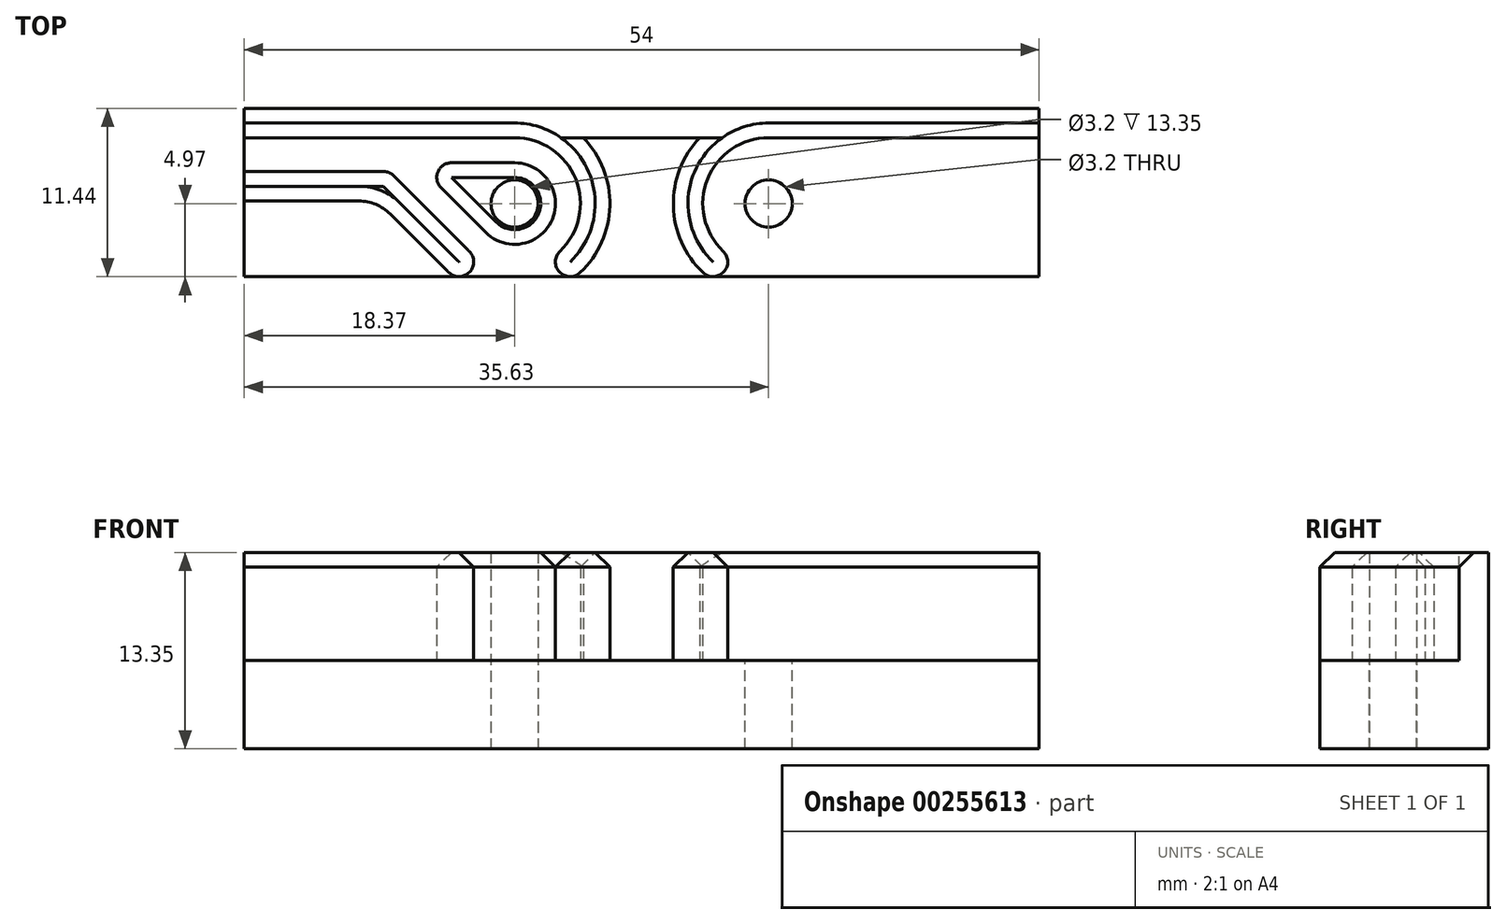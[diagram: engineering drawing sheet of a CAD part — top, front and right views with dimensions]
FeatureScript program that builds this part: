
annotation { "Feature Type Name" : "Feature", "Feature Type Description" : "" }
export const myFeature = defineFeature(function(context is Context, id is Id, definition is map)
    precondition{}
    {
        {
            var Q0;
            Q0=qCreatedBy(makeId("Top.planeOp"),FACE);
            cPlane(context, id + "F0", {"entities" : qUnion([Q0]), "cplaneType" : CPlaneType.OFFSET, "offset" : 6 * mm, "width" : 150 * mm, "height" : 150 * mm});
        }
        {
            var Q0;
            Q0=qCreatedBy(id+"F0.planeOp",FACE);
            var sketch = newSketch(context, id + "F1", { "sketchPlane" : qUnion([Q0])});
            skLineSegment(sketch, "E0.bottom", {"start": v(-27, 6.48) * mm, "end": v(27, 6.48) * mm});
            skLineSegment(sketch, "E0.top", {"start": v(-27, 4.48) * mm, "end": v(-8.63, 4.48) * mm});
            skLineSegment(sketch, "E0.left", {"start": v(-27, 6.48) * mm, "end": v(-27, 4.48) * mm});
            skLineSegment(sketch, "E0.right", {"start": v(27, 6.48) * mm, "end": v(27, 4.48) * mm});
            skArc(sketch, "E1", {"start": v(-10.6, -1.96) * mm, "mid": v(-6.07, -1.06) * mm, "end": v(-8.63, 2.77) * mm});
            skArc(sketch, "E2.MirrorC", {"start": v(10.6, -1.96) * mm, "mid": v(6.07, -1.06) * mm, "end": v(8.63, 2.77) * mm});
            skLineSegment(sketch, "E3", {"start": v(-8.63, 2.77) * mm, "end": v(-12.92, 2.77) * mm});
            skLineSegment(sketch, "E4", {"start": v(-13.62, 1.07) * mm, "end": v(-10.6, -1.96) * mm});
            skArc(sketch, "E5", {"start": v(-12.92, 2.77) * mm, "mid": v(-13.84, 2.16) * mm, "end": v(-13.62, 1.07) * mm});
            skLineSegment(sketch, "E6.MirrorCS", {"start": v(8.63, 2.77) * mm, "end": v(12.92, 2.77) * mm});
            skArc(sketch, "E7.MirrorCS", {"start": v(12.92, 2.77) * mm, "mid": v(13.84, 2.16) * mm, "end": v(13.62, 1.07) * mm});
            skLineSegment(sketch, "E8.MirrorCS", {"start": v(13.62, 1.07) * mm, "end": v(10.6, -1.96) * mm});
            skCircle(sketch, "E9", {"center": v(-8.63, 0) * mm, "radius": 1.6 * mm});
            skCircle(sketch, "E10", {"center": v(8.63, 0) * mm, "radius": 1.6 * mm});
            skLineSegment(sketch, "E11", {"start": v(-27, 2.18) * mm, "end": v(-17.55, 2.18) * mm});
            skLineSegment(sketch, "E12", {"start": v(-16.84, 1.88) * mm, "end": v(-11.8, -3.16) * mm});
            skLineSegment(sketch, "E13", {"start": v(-13.2, -4.58) * mm, "end": v(-17.08, -0.7) * mm});
            skLineSegment(sketch, "E14", {"start": v(-19.2, 0.17) * mm, "end": v(-27, 0.17) * mm});
            skLineSegment(sketch, "E15", {"start": v(-27, 0.17) * mm, "end": v(-27, 2.18) * mm});
            skArc(sketch, "E16", {"start": v(-11.8, -3.16) * mm, "mid": v(-11.76, -3.2) * mm, "end": v(-11.72, -3.24) * mm});
            skArc(sketch, "E17", {"start": v(-13.2, -4.58) * mm, "mid": v(-13.15, -4.63) * mm, "end": v(-13.1, -4.69) * mm});
            skLineSegment(sketch, "E18.trimOffspring", {"start": v(-3.95, 4.48) * mm, "end": v(3.95, 4.48) * mm});
            skPoint(sketch, "E19.visualSharp", {"position": v(-17.13, 2.18) * mm});
            skArc(sketch, "E19.filletArc", {"start": v(-16.84, 1.88) * mm, "mid": v(-17.17, 2.1) * mm, "end": v(-17.55, 2.18) * mm});
            skPoint(sketch, "E20.visualSharp", {"position": v(-17.96, 0.17) * mm});
            skArc(sketch, "E20.filletArc", {"start": v(-17.08, -0.7) * mm, "mid": v(-18.06, -0.05) * mm, "end": v(-19.2, 0.17) * mm});
            skArc(sketch, "E21.MirrorCS", {"start": v(13.2, -4.58) * mm, "mid": v(13.15, -4.63) * mm, "end": v(13.1, -4.69) * mm});
            skArc(sketch, "E22.MirrorCS", {"start": v(11.8, -3.16) * mm, "mid": v(11.76, -3.2) * mm, "end": v(11.72, -3.24) * mm});
            skLineSegment(sketch, "E23.MirrorCS", {"start": v(16.84, 1.88) * mm, "end": v(11.8, -3.16) * mm});
            skLineSegment(sketch, "E24.MirrorCS", {"start": v(13.2, -4.58) * mm, "end": v(17.08, -0.7) * mm});
            skArc(sketch, "E25.MirrorCS", {"start": v(17.08, -0.7) * mm, "mid": v(18.06, -0.05) * mm, "end": v(19.2, 0.17) * mm});
            skLineSegment(sketch, "E26.MirrorCS", {"start": v(27, 2.18) * mm, "end": v(17.55, 2.18) * mm});
            skLineSegment(sketch, "E27.MirrorCS", {"start": v(27, 0.17) * mm, "end": v(27, 2.18) * mm});
            skLineSegment(sketch, "E28.MirrorCS", {"start": v(19.2, 0.17) * mm, "end": v(27, 0.17) * mm});
            skArc(sketch, "E29.MirrorCS", {"start": v(16.84, 1.88) * mm, "mid": v(17.17, 2.1) * mm, "end": v(17.55, 2.18) * mm});
            skLineSegment(sketch, "E30.trimOffspring", {"start": v(8.63, 4.48) * mm, "end": v(27, 4.48) * mm});
            skArc(sketch, "E31", {"start": v(-5.54, -3.24) * mm, "mid": v(-5.58, -4.65) * mm, "end": v(-4.17, -4.69) * mm});
            skLineSegment(sketch, "E32", {"start": v(-5.86, 0) * mm, "end": v(-5.86, -10.37) * mm, "construction": true});
            skLineSegment(sketch, "E33", {"start": v(-8.63, 0) * mm, "end": v(-8.63, -10.25) * mm, "construction": true});
            skArc(sketch, "E34.MirrorCS", {"start": v(-11.72, -3.24) * mm, "mid": v(-11.68, -4.65) * mm, "end": v(-13.1, -4.69) * mm});
            skArc(sketch, "E35.trimOffspring", {"start": v(-5.54, -3.24) * mm, "mid": v(-4.47, 1.66) * mm, "end": v(-8.63, 4.48) * mm});
            skArc(sketch, "E36.trimOffspring", {"start": v(-5.86, -5.85) * mm, "mid": v(-2.26, -1.17) * mm, "end": v(-3.95, 4.48) * mm});
            skArc(sketch, "E37.MirrorCS", {"start": v(11.72, -3.24) * mm, "mid": v(11.68, -4.65) * mm, "end": v(13.1, -4.69) * mm});
            skArc(sketch, "E38.MirrorCS", {"start": v(5.54, -3.24) * mm, "mid": v(5.58, -4.65) * mm, "end": v(4.17, -4.69) * mm});
            skArc(sketch, "E39.trimOffspring", {"start": v(5.54, -3.24) * mm, "mid": v(4.47, 1.66) * mm, "end": v(8.63, 4.48) * mm});
            skArc(sketch, "E40.trimOffspring", {"start": v(4.17, -4.69) * mm, "mid": v(2.16, -0.15) * mm, "end": v(3.95, 4.48) * mm});
            skSolve(sketch);
        }
        {
            var Q0;
            Q0=makeQuery(id+"F1.imprint","IMPRINT",FACE,{"disambiguationData":[TD([[makeQuery(id+"F1.imprint","IMPRINT",EDGE,{"derivedFrom":sQuery(id+"F1.wireOp",EDGE,"E0.bottom")}),-1.0]])]});
            var Q1;
            Q1=makeQuery(id+"F1.imprint","IMPRINT",FACE,{"disambiguationData":[TD([[makeQuery(id+"F1.imprint","IMPRINT",EDGE,{"derivedFrom":sQuery(id+"F1.wireOp",EDGE,"E1")}),1.0]])]});
            var Q2;
            Q2=makeQuery(id+"F1.imprint","IMPRINT",FACE,{"disambiguationData":[TD([[makeQuery(id+"F1.imprint","IMPRINT",EDGE,{"derivedFrom":sQuery(id+"F1.wireOp",EDGE,"E2.MirrorC")}),-1.0]])]});
            var Q3;
            Q3=makeQuery(id+"F1.imprint","IMPRINT",FACE,{"disambiguationData":[TD([[makeQuery(id+"F1.imprint","IMPRINT",EDGE,{"derivedFrom":sQuery(id+"F1.wireOp",EDGE,"E11")}),-1.0]])]});
            var Q4;
            Q4=makeQuery(id+"F1.imprint","IMPRINT",FACE,{"disambiguationData":[TD([[makeQuery(id+"F1.imprint","IMPRINT",EDGE,{"derivedFrom":sQuery(id+"F1.wireOp",EDGE,"E21.MirrorCS")}),-1.0]])]});
            extrude(context, id + "F2", {"entities" : qUnion([Q0, Q1, Q2, Q3, Q4]), "depth" : 7.35 * mm});
        }
        {
            var Q0;
            Q0=makeQuery(id+"F2.opExtrude","CAP_FACE",FACE,{"disambiguationData":[OSD([sQuery(id+"F1.wireOp",EDGE,"E0.bottom"),sQuery(id+"F1.wireOp",EDGE,"E0.top"),sQuery(id+"F1.wireOp",EDGE,"E0.left"),sQuery(id+"F1.wireOp",EDGE,"E0.right"),sQuery(id+"F1.wireOp",EDGE,"E11"),sQuery(id+"F1.wireOp",EDGE,"E12"),sQuery(id+"F1.wireOp",EDGE,"E13"),sQuery(id+"F1.wireOp",EDGE,"E14"),sQuery(id+"F1.wireOp",EDGE,"E15"),sQuery(id+"F1.wireOp",EDGE,"E16"),sQuery(id+"F1.wireOp",EDGE,"E17"),sQuery(id+"F1.wireOp",EDGE,"E18.trimOffspring"),sQuery(id+"F1.wireOp",EDGE,"E19.filletArc"),sQuery(id+"F1.wireOp",EDGE,"E20.filletArc"),sQuery(id+"F1.wireOp",EDGE,"E21.MirrorCS"),sQuery(id+"F1.wireOp",EDGE,"E22.MirrorCS"),sQuery(id+"F1.wireOp",EDGE,"E23.MirrorCS"),sQuery(id+"F1.wireOp",EDGE,"E24.MirrorCS"),sQuery(id+"F1.wireOp",EDGE,"E25.MirrorCS"),sQuery(id+"F1.wireOp",EDGE,"E26.MirrorCS"),sQuery(id+"F1.wireOp",EDGE,"E27.MirrorCS"),sQuery(id+"F1.wireOp",EDGE,"E28.MirrorCS"),sQuery(id+"F1.wireOp",EDGE,"E29.MirrorCS"),sQuery(id+"F1.wireOp",EDGE,"E30.trimOffspring")])],"isStart":true});
            var sketch = newSketch(context, id + "F3", { "sketchPlane" : qUnion([Q0])});
            skLineSegment(sketch, "E41.bottom", {"start": v(27, -6.48) * mm, "end": v(-27, -6.48) * mm});
            skLineSegment(sketch, "E41.top", {"start": v(27, 4.97) * mm, "end": v(-27, 4.97) * mm});
            skLineSegment(sketch, "E41.left", {"start": v(27, -6.48) * mm, "end": v(27, 4.97) * mm});
            skLineSegment(sketch, "E41.right", {"start": v(-27, -6.48) * mm, "end": v(-27, 4.97) * mm});
            skCircle(sketch, "E42.0", {"center": v(-8.63, 0) * mm, "radius": 1.6 * mm});
            skCircle(sketch, "E43.0", {"center": v(8.63, 0) * mm, "radius": 1.6 * mm});
            skSolve(sketch);
        }
        {
            var Q0;
            Q0 = qSketchRegion(id + "F3", true);
            var Q1;
            Q1=qCreatedBy(makeId("Top.planeOp"),FACE);
            extrude(context, id + "F4", {"entities" : qUnion([Q0]), "operationType" : NewBodyOperationType.ADD, "endBound" : BoundingType.UP_TO_SURFACE, "endBoundEntityFace" : qUnion([Q1]), "depth" : 25 * mm});
        }
        {
            var Q0;
            Q0=makeQuery(id+"F2.opExtrude","CAP_EDGE",EDGE,{"disambiguationData":[OSD([sQuery(id+"F1.wireOp",EDGE,"E11")])],"isStart":false});
            var Q1;
            Q1=makeQuery(id+"F2.opExtrude","CAP_EDGE",EDGE,{"disambiguationData":[OSD([sQuery(id+"F1.wireOp",EDGE,"E0.top")])],"isStart":false});
            var Q2;
            Q2=makeQuery(id+"F2.opExtrude","CAP_EDGE",EDGE,{"disambiguationData":[OSD([sQuery(id+"F1.wireOp",EDGE,"E30.trimOffspring")])],"isStart":false});
            var Q3;
            Q3=makeQuery(id+"F2.opExtrude","CAP_EDGE",EDGE,{"disambiguationData":[OSD([sQuery(id+"F1.wireOp",EDGE,"E26.MirrorCS")])],"isStart":false});
            var Q4;
            Q4=makeQuery(id+"F2.opExtrude","CAP_EDGE",EDGE,{"disambiguationData":[OSD([sQuery(id+"F1.wireOp",EDGE,"E3")])],"isStart":false});
            var Q5;
            Q5=makeQuery(id+"F2.opExtrude","CAP_EDGE",EDGE,{"disambiguationData":[OSD([sQuery(id+"F1.wireOp",EDGE,"E6.MirrorCS")])],"isStart":false});
            chamfer(context, id + "F5", {"entities" : qUnion([Q0, Q1, Q2, Q3, Q4, Q5]), "width" : 1 * mm, "tangentPropagation" : true});
        }
    });
